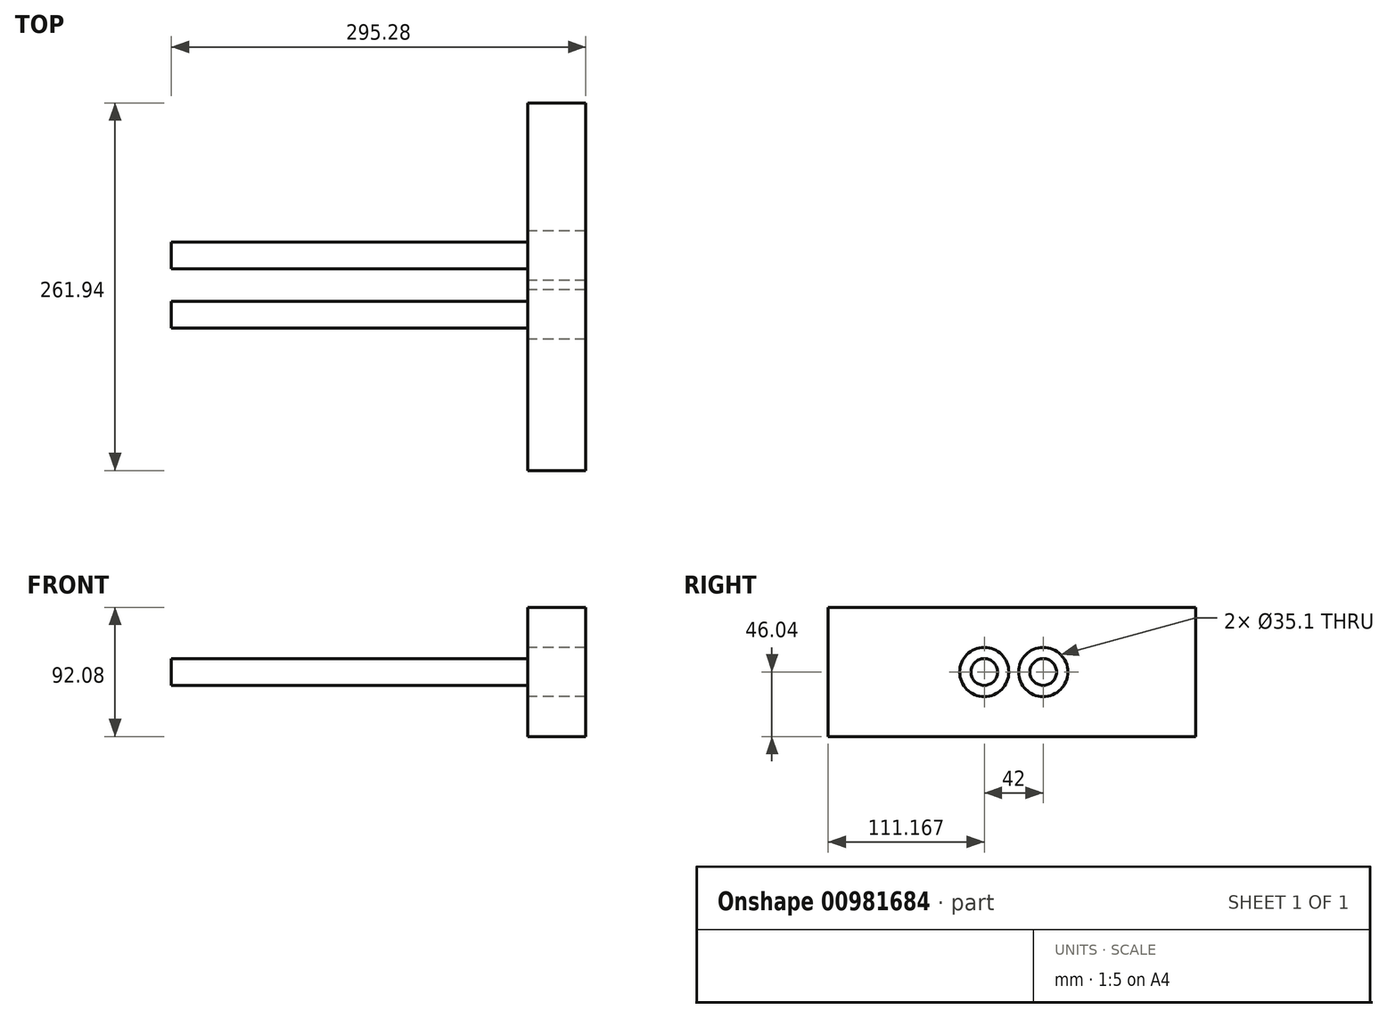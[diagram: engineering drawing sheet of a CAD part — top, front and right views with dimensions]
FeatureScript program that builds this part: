
annotation { "Feature Type Name" : "Feature", "Feature Type Description" : "" }
export const myFeature = defineFeature(function(context is Context, id is Id, definition is map)
    precondition{}
    {
        {
            var Q0;
            Q0=qCreatedBy(makeId("Right.planeOp"),FACE);
            var sketch = newSketch(context, id + "F0", { "sketchPlane" : qUnion([Q0])});
            skCircle(sketch, "E0", {"center": v(-44.93, 0) * mm, "radius": 9.53 * mm});
            skCircle(sketch, "E1", {"center": v(-2.93, 0) * mm, "radius": 9.53 * mm});
            skSolve(sketch);
        }
        {
            var Q0;
            Q0 = qSketchRegion(id + "F0", true);
            extrude(context, id + "F1", {"entities" : qUnion([Q0]), "oppositeDirection" : true, "depth" : 254 * mm, "offsetDistance" : 25 * mm});
        }
        {
            var Q0;
            Q0=qCreatedBy(makeId("Right.planeOp"),FACE);
            var sketch = newSketch(context, id + "F2", { "sketchPlane" : qUnion([Q0])});
            skCircle(sketch, "E2", {"center": v(-44.93, 0) * mm, "radius": 17.55 * mm});
            skCircle(sketch, "E3", {"center": v(-2.93, 0) * mm, "radius": 17.55 * mm});
            skSolve(sketch);
        }
        {
            var Q0;
            Q0=qCreatedBy(makeId("Right.planeOp"),FACE);
            var sketch = newSketch(context, id + "F3", { "sketchPlane" : qUnion([Q0])});
            skLineSegment(sketch, "E4.bottom", {"start": v(105.84, -46.04) * mm, "end": v(-156.1, -46.04) * mm});
            skLineSegment(sketch, "E4.top", {"start": v(105.84, 46.04) * mm, "end": v(-156.1, 46.04) * mm});
            skLineSegment(sketch, "E4.left", {"start": v(105.84, -46.04) * mm, "end": v(105.84, 46.04) * mm});
            skLineSegment(sketch, "E4.right", {"start": v(-156.1, -46.04) * mm, "end": v(-156.1, 46.04) * mm});
            skPoint(sketch, "E4.middle", {"position": v(-25.13, 0) * mm});
            skSolve(sketch);
        }
        {
            var Q0;
            Q0 = qSketchRegion(id + "F3", true);
            extrude(context, id + "F4", {"entities" : qUnion([Q0]), "depth" : 41.27 * mm, "offsetDistance" : 25 * mm});
        }
        {
            var Q0;
            Q0 = qSketchRegion(id + "F2", true);
            extrude(context, id + "F5", {"entities" : qUnion([Q0]), "operationType" : NewBodyOperationType.REMOVE, "depth" : 65.2 * mm, "offsetDistance" : 25 * mm});
        }
    });
